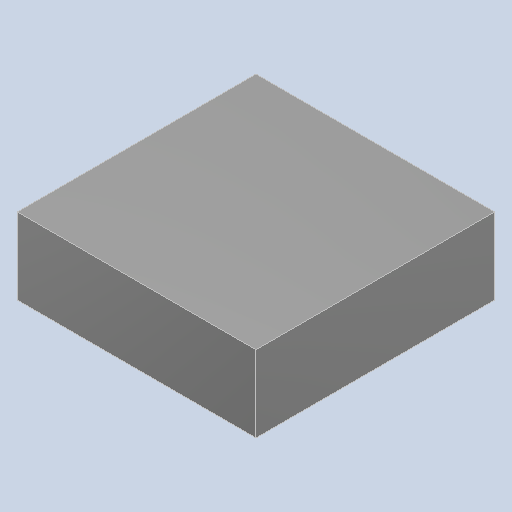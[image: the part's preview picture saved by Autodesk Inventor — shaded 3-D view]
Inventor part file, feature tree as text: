
AUTODESK INVENTOR PART (.ipt)
format: ipt  version: 2022 (Build 260153000, 153)  size: 85,504 bytes
history: imported  units: in
note: dims shown in document units (in); Inventor stores cm internally (conversion verified against a paired STEP export)
features: imported_body x1
ambient origin geometry x8: Origin, YZ Plane, XZ Plane, XY Plane, X Axis, Y Axis, Z Axis, Center Point
bodies: Solid1 (imported_parasolid)
feature tree (1):
  imported_body  NMx_Import_Brep_tag  [imported B-rep: ~6 faces, bbox_mm=[2.5, 0.8, 2.5]]
